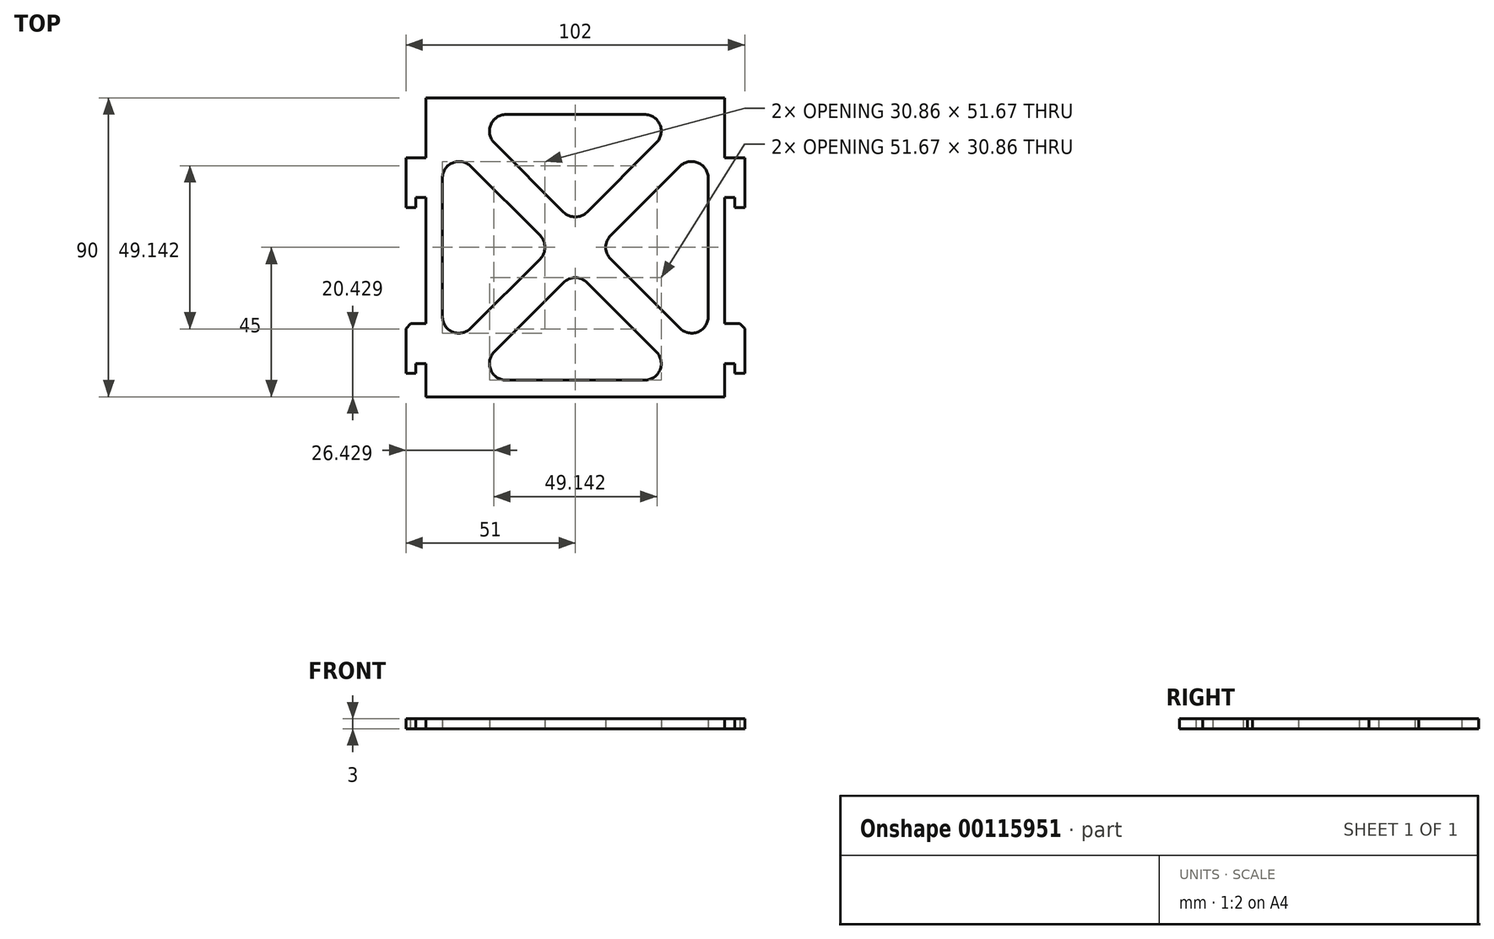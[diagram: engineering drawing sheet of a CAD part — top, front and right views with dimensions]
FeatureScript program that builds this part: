
annotation { "Feature Type Name" : "Feature", "Feature Type Description" : "" }
export const myFeature = defineFeature(function(context is Context, id is Id, definition is map)
    precondition{}
    {
        {
            var Q0;
            Q0=qCreatedBy(makeId("Top.planeOp"),FACE);
            var sketch = newSketch(context, id + "F0", { "sketchPlane" : qUnion([Q0])});
            skLineSegment(sketch, "E0.bottom", {"start": v(45, -45) * mm, "end": v(-45, -45) * mm});
            skLineSegment(sketch, "E0.top", {"start": v(45, 45) * mm, "end": v(-45, 45) * mm});
            skLineSegment(sketch, "E0.left", {"start": v(45, -45) * mm, "end": v(45, 45) * mm});
            skLineSegment(sketch, "E0.right", {"start": v(-45, -45) * mm, "end": v(-45, 45) * mm});
            skPoint(sketch, "E0.middle", {"position": v(0, 0) * mm});
            skLineSegment(sketch, "E1", {"start": v(-45, 45) * mm, "end": v(45, -45) * mm, "construction": true});
            skLineSegment(sketch, "E2", {"start": v(45, 45) * mm, "end": v(-45, -45) * mm, "construction": true});
            skLineSegment(sketch, "E3.0", {"start": v(-31.46, 24.4) * mm, "end": v(-10.6, 3.54) * mm});
            skLineSegment(sketch, "E4.0", {"start": v(-40, -20.86) * mm, "end": v(-40, 20.86) * mm});
            skLineSegment(sketch, "E5.0", {"start": v(-10.6, -3.54) * mm, "end": v(-31.46, -24.4) * mm});
            skArc(sketch, "E6.filletArc", {"start": v(-31.46, 24.4) * mm, "mid": v(-36.91, 25.48) * mm, "end": v(-40, 20.86) * mm});
            skArc(sketch, "E7.filletArc", {"start": v(-10.6, -3.54) * mm, "mid": v(-9.14, 0) * mm, "end": v(-10.6, 3.54) * mm});
            skArc(sketch, "E8.filletArc", {"start": v(-40, -20.86) * mm, "mid": v(-36.91, -25.48) * mm, "end": v(-31.46, -24.4) * mm});
            skLineSegment(sketch, "E9.0", {"start": v(24.4, 31.46) * mm, "end": v(3.54, 10.6) * mm});
            skLineSegment(sketch, "E10.0", {"start": v(-24.4, 31.46) * mm, "end": v(-3.54, 10.6) * mm});
            skLineSegment(sketch, "E11.0", {"start": v(20.86, 40) * mm, "end": v(-20.86, 40) * mm});
            skArc(sketch, "E12.filletArc", {"start": v(-20.86, 40) * mm, "mid": v(-25.48, 36.91) * mm, "end": v(-24.4, 31.46) * mm});
            skArc(sketch, "E13.filletArc", {"start": v(24.4, 31.46) * mm, "mid": v(25.48, 36.91) * mm, "end": v(20.86, 40) * mm});
            skArc(sketch, "E14.filletArc", {"start": v(-3.54, 10.6) * mm, "mid": v(0, 9.14) * mm, "end": v(3.54, 10.6) * mm});
            skLineSegment(sketch, "E15.MirrorCS", {"start": v(24.4, -31.46) * mm, "end": v(3.54, -10.6) * mm});
            skLineSegment(sketch, "E16.MirrorCS", {"start": v(-24.4, -31.46) * mm, "end": v(-3.54, -10.6) * mm});
            skArc(sketch, "E17.MirrorCS", {"start": v(-3.54, -10.6) * mm, "mid": v(0, -9.14) * mm, "end": v(3.54, -10.6) * mm});
            skArc(sketch, "E18.MirrorCS", {"start": v(-20.86, -40) * mm, "mid": v(-25.48, -36.91) * mm, "end": v(-24.4, -31.46) * mm});
            skLineSegment(sketch, "E19.MirrorCS", {"start": v(20.86, -40) * mm, "end": v(-20.86, -40) * mm});
            skArc(sketch, "E20.MirrorCS", {"start": v(24.4, -31.46) * mm, "mid": v(25.48, -36.91) * mm, "end": v(20.86, -40) * mm});
            skLineSegment(sketch, "E21.MirrorCS", {"start": v(31.46, 24.4) * mm, "end": v(10.6, 3.54) * mm});
            skArc(sketch, "E22.MirrorCS", {"start": v(31.46, 24.4) * mm, "mid": v(36.91, 25.48) * mm, "end": v(40, 20.86) * mm});
            skLineSegment(sketch, "E23.MirrorCS", {"start": v(40, -20.86) * mm, "end": v(40, 20.86) * mm});
            skArc(sketch, "E24.MirrorCS", {"start": v(40, -20.86) * mm, "mid": v(36.91, -25.48) * mm, "end": v(31.46, -24.4) * mm});
            skLineSegment(sketch, "E25.MirrorCS", {"start": v(10.6, -3.54) * mm, "end": v(31.46, -24.4) * mm});
            skArc(sketch, "E26.MirrorCS", {"start": v(10.6, -3.54) * mm, "mid": v(9.14, 0) * mm, "end": v(10.6, 3.54) * mm});
            skSolve(sketch);
        }
        {
            var Q0;
            Q0=makeQuery(id+"F0.imprint","IMPRINT",FACE,{"disambiguationData":[TD([[makeQuery(id+"F0.imprint","IMPRINT",EDGE,{"derivedFrom":sQuery(id+"F0.wireOp",EDGE,"E0.bottom")}),-1.0]])]});
            extrude(context, id + "F1", {"entities" : qUnion([Q0]), "depth" : 3 * mm});
        }
        {
            var Q0;
            Q0=makeQuery(id+"F1.opExtrude","CAP_FACE",FACE,{"disambiguationData":[OSD([sQuery(id+"F0.wireOp",EDGE,"E0.bottom"),sQuery(id+"F0.wireOp",EDGE,"E0.top"),sQuery(id+"F0.wireOp",EDGE,"E0.left"),sQuery(id+"F0.wireOp",EDGE,"E0.right"),sQuery(id+"F0.wireOp",EDGE,"E3.0"),sQuery(id+"F0.wireOp",EDGE,"E4.0"),sQuery(id+"F0.wireOp",EDGE,"E5.0"),sQuery(id+"F0.wireOp",EDGE,"E6.filletArc"),sQuery(id+"F0.wireOp",EDGE,"E7.filletArc"),sQuery(id+"F0.wireOp",EDGE,"E8.filletArc"),sQuery(id+"F0.wireOp",EDGE,"E9.0"),sQuery(id+"F0.wireOp",EDGE,"E10.0"),sQuery(id+"F0.wireOp",EDGE,"E11.0"),sQuery(id+"F0.wireOp",EDGE,"E12.filletArc"),sQuery(id+"F0.wireOp",EDGE,"E13.filletArc"),sQuery(id+"F0.wireOp",EDGE,"E14.filletArc"),sQuery(id+"F0.wireOp",EDGE,"E15.MirrorCS"),sQuery(id+"F0.wireOp",EDGE,"E16.MirrorCS"),sQuery(id+"F0.wireOp",EDGE,"E17.MirrorCS"),sQuery(id+"F0.wireOp",EDGE,"E18.MirrorCS"),sQuery(id+"F0.wireOp",EDGE,"E19.MirrorCS"),sQuery(id+"F0.wireOp",EDGE,"E20.MirrorCS"),sQuery(id+"F0.wireOp",EDGE,"E21.MirrorCS"),sQuery(id+"F0.wireOp",EDGE,"E22.MirrorCS"),sQuery(id+"F0.wireOp",EDGE,"E23.MirrorCS"),sQuery(id+"F0.wireOp",EDGE,"E24.MirrorCS"),sQuery(id+"F0.wireOp",EDGE,"E25.MirrorCS"),sQuery(id+"F0.wireOp",EDGE,"E26.MirrorCS")])],"isStart":true});
            var sketch = newSketch(context, id + "F2", { "sketchPlane" : qUnion([Q0])});
            skLineSegment(sketch, "E27.bottom", {"start": v(45, -27) * mm, "end": v(51, -27) * mm});
            skLineSegment(sketch, "E27.top", {"start": v(48, -12) * mm, "end": v(51, -12) * mm});
            skLineSegment(sketch, "E27.left", {"start": v(45, -27) * mm, "end": v(45, -15) * mm});
            skLineSegment(sketch, "E27.right", {"start": v(51, -27) * mm, "end": v(51, -12) * mm});
            skLineSegment(sketch, "E28.bottom", {"start": v(45, -15) * mm, "end": v(48, -15) * mm});
            skLineSegment(sketch, "E28.right", {"start": v(48, -15) * mm, "end": v(48, -12) * mm});
            skPoint(sketch, "E29.orphan", {"position": v(45, -12) * mm});
            skLineSegment(sketch, "E30.bottom", {"start": v(45, 23) * mm, "end": v(51, 23) * mm});
            skLineSegment(sketch, "E30.top", {"start": v(48, 38) * mm, "end": v(51, 38) * mm});
            skLineSegment(sketch, "E30.left", {"start": v(45, 23) * mm, "end": v(45, 35) * mm});
            skLineSegment(sketch, "E30.right", {"start": v(51, 23) * mm, "end": v(51, 38) * mm});
            skLineSegment(sketch, "E31.bottom", {"start": v(45, 35) * mm, "end": v(48, 35) * mm});
            skLineSegment(sketch, "E31.right", {"start": v(48, 35) * mm, "end": v(48, 38) * mm});
            skPoint(sketch, "E32.orphan", {"position": v(45, 38) * mm});
            skLineSegment(sketch, "E33.MirrorCS", {"start": v(-48, -15) * mm, "end": v(-48, -12) * mm});
            skLineSegment(sketch, "E34.MirrorCS", {"start": v(-45, -15) * mm, "end": v(-48, -15) * mm});
            skLineSegment(sketch, "E35.MirrorCS", {"start": v(-48, -12) * mm, "end": v(-51, -12) * mm});
            skLineSegment(sketch, "E36.MirrorCS", {"start": v(-45, 35) * mm, "end": v(-48, 35) * mm});
            skLineSegment(sketch, "E37.MirrorCS", {"start": v(-48, 35) * mm, "end": v(-48, 38) * mm});
            skLineSegment(sketch, "E38.MirrorCS", {"start": v(-48, 38) * mm, "end": v(-51, 38) * mm});
            skLineSegment(sketch, "E39.MirrorCS", {"start": v(-45, 23) * mm, "end": v(-51, 23) * mm});
            skLineSegment(sketch, "E40.MirrorCS", {"start": v(-51, -27) * mm, "end": v(-51, -12) * mm});
            skLineSegment(sketch, "E41.MirrorCS", {"start": v(-45, -27) * mm, "end": v(-45, -15) * mm});
            skLineSegment(sketch, "E42.MirrorCS", {"start": v(-45, -27) * mm, "end": v(-51, -27) * mm});
            skLineSegment(sketch, "E43.MirrorCS", {"start": v(-45, 23) * mm, "end": v(-45, 35) * mm});
            skLineSegment(sketch, "E44.MirrorCS", {"start": v(-51, 23) * mm, "end": v(-51, 38) * mm});
            skPoint(sketch, "E45.MirrorP", {"position": v(-45, -12) * mm});
            skPoint(sketch, "E46.MirrorP", {"position": v(-45, 38) * mm});
            skSolve(sketch);
        }
        {
            var Q0;
            Q0 = qSketchRegion(id + "F2", true);
            var Q1;
            Q1=makeQuery(id+"F1.opExtrude","CAP_FACE",FACE,{"disambiguationData":[OSD([sQuery(id+"F0.wireOp",EDGE,"E0.bottom"),sQuery(id+"F0.wireOp",EDGE,"E0.top"),sQuery(id+"F0.wireOp",EDGE,"E0.left"),sQuery(id+"F0.wireOp",EDGE,"E0.right"),sQuery(id+"F0.wireOp",EDGE,"E3.0"),sQuery(id+"F0.wireOp",EDGE,"E4.0"),sQuery(id+"F0.wireOp",EDGE,"E5.0"),sQuery(id+"F0.wireOp",EDGE,"E6.filletArc"),sQuery(id+"F0.wireOp",EDGE,"E7.filletArc"),sQuery(id+"F0.wireOp",EDGE,"E8.filletArc"),sQuery(id+"F0.wireOp",EDGE,"E9.0"),sQuery(id+"F0.wireOp",EDGE,"E10.0"),sQuery(id+"F0.wireOp",EDGE,"E11.0"),sQuery(id+"F0.wireOp",EDGE,"E12.filletArc"),sQuery(id+"F0.wireOp",EDGE,"E13.filletArc"),sQuery(id+"F0.wireOp",EDGE,"E14.filletArc"),sQuery(id+"F0.wireOp",EDGE,"E15.MirrorCS"),sQuery(id+"F0.wireOp",EDGE,"E16.MirrorCS"),sQuery(id+"F0.wireOp",EDGE,"E17.MirrorCS"),sQuery(id+"F0.wireOp",EDGE,"E18.MirrorCS"),sQuery(id+"F0.wireOp",EDGE,"E19.MirrorCS"),sQuery(id+"F0.wireOp",EDGE,"E20.MirrorCS"),sQuery(id+"F0.wireOp",EDGE,"E21.MirrorCS"),sQuery(id+"F0.wireOp",EDGE,"E22.MirrorCS"),sQuery(id+"F0.wireOp",EDGE,"E23.MirrorCS"),sQuery(id+"F0.wireOp",EDGE,"E24.MirrorCS"),sQuery(id+"F0.wireOp",EDGE,"E25.MirrorCS"),sQuery(id+"F0.wireOp",EDGE,"E26.MirrorCS")])],"isStart":false});
            extrude(context, id + "F3", {"entities" : qUnion([Q0]), "operationType" : NewBodyOperationType.ADD, "endBound" : BoundingType.UP_TO_SURFACE, "oppositeDirection" : true, "endBoundEntityFace" : qUnion([Q1]), "depth" : 25 * mm});
        }
        {
            var Q0;
            Q0=makeQuery(id+"F3.opExtrude","SWEPT_EDGE",EDGE,{"disambiguationData":[OSD([sQuery(id+"F2.wireOp",EDGE,"E39.MirrorCS"),sQuery(id+"F2.wireOp",EDGE,"E44.MirrorCS")])]});
            var Q1;
            Q1=makeQuery(id+"F3.opExtrude","SWEPT_EDGE",EDGE,{"disambiguationData":[OSD([sQuery(id+"F2.wireOp",EDGE,"E30.bottom"),sQuery(id+"F2.wireOp",EDGE,"E30.right")])]});
            chamfer(context, id + "F4", {"entities" : qUnion([Q0, Q1]), "width" : 1.5 * mm, "tangentPropagation" : true});
        }
    });
